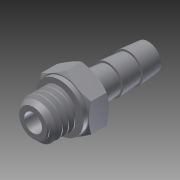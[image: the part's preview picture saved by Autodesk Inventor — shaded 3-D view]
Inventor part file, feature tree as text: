
AUTODESK INVENTOR PART (.ipt)
format: ipt  version: 2012 SP1 (Build 160190100, 190)  size: 515,584 bytes
history: native  units: in
note: dims shown in document units (in); Inventor stores cm internally (conversion verified against a paired STEP export)
features: other x2, imported_body x2, extrude x1, sketch x1
ambient origin geometry x8: Origin, YZ Plane, XZ Plane, XY Plane, X Axis, Y Axis, Z Axis, Center Point
feature tree (6):
  parser-record x1  (decoder bookkeeping rows leaked as tree rows — omitted from the tree; the rows remain in map.json)
  imported_body  "Base1"
  imported_body  "Base2"
  extrude  "Extrusion1"  [1 undecoded]
  other  "NONE_1"
  sketch  "Sketch2"  dims[d0=0.0in d1=0.0in]
note: 1 required parameter value undecoded (feature->parameter linkage not recoverable at this tier; creation-order binding heuristic only, values carry confidence <= 0.55)
